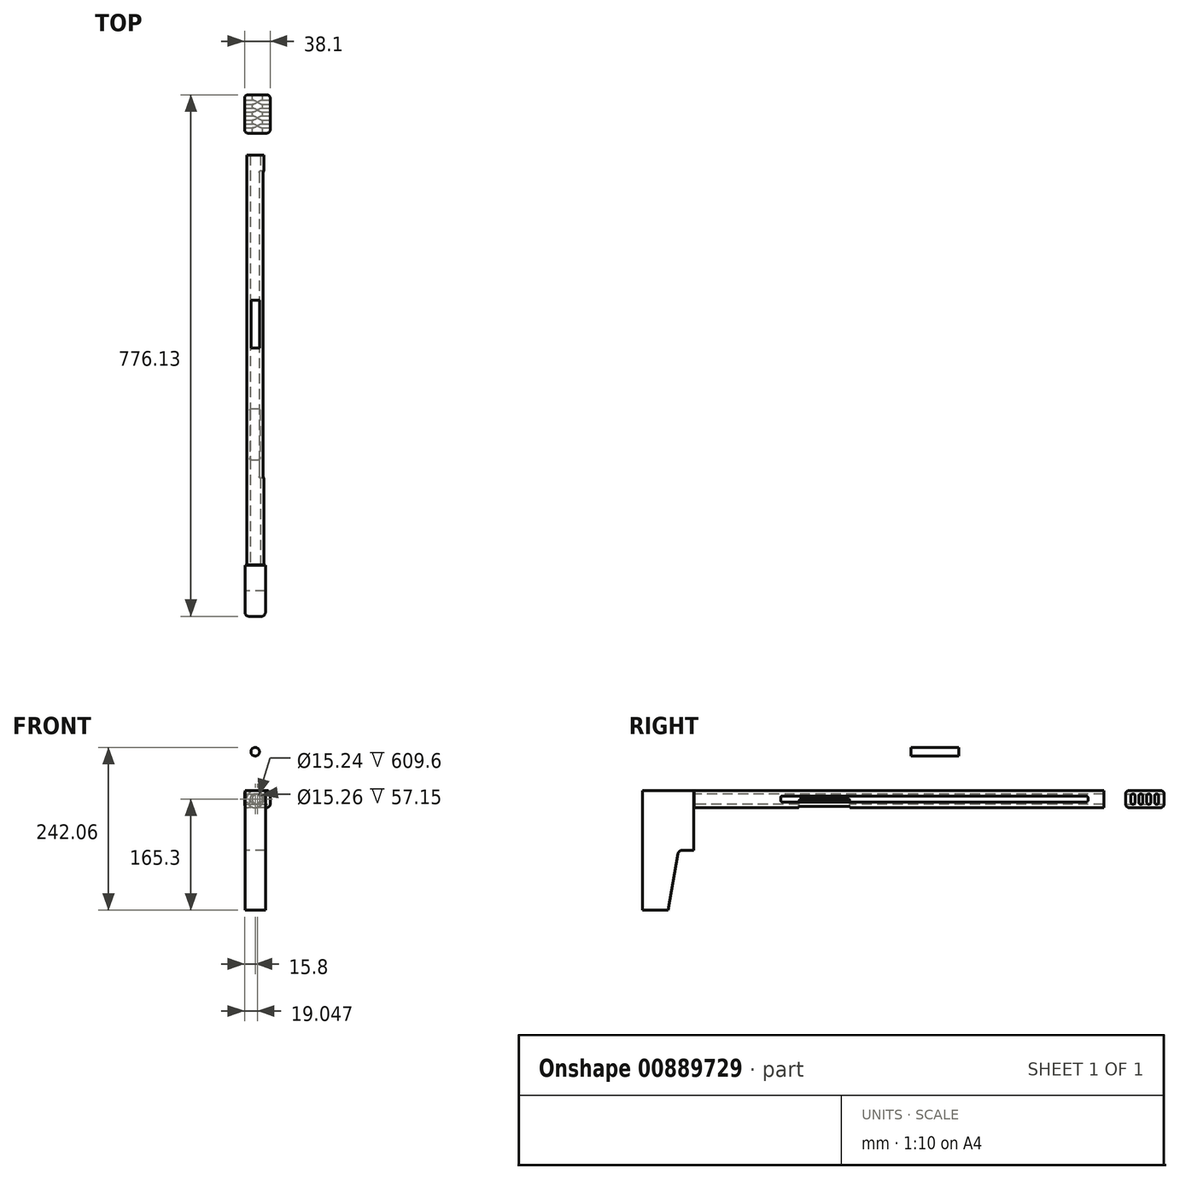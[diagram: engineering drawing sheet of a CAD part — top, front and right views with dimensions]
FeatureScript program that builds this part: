
annotation { "Feature Type Name" : "Feature", "Feature Type Description" : "" }
export const myFeature = defineFeature(function(context is Context, id is Id, definition is map)
    precondition{}
    {
        {
            var Q0;
            Q0=qCreatedBy(makeId("Right.planeOp"),FACE);
            var sketch = newSketch(context, id + "F0", { "sketchPlane" : qUnion([Q0])});
            skLineSegment(sketch, "E0.bottom", {"start": v(-36.5, 76.76) * mm, "end": v(34.62, 76.76) * mm});
            skLineSegment(sketch, "E0.top", {"start": v(-36.5, 64.06) * mm, "end": v(34.62, 64.06) * mm});
            skLineSegment(sketch, "E0.left", {"start": v(-36.5, 76.76) * mm, "end": v(-36.5, 64.06) * mm});
            skLineSegment(sketch, "E0.right", {"start": v(34.62, 76.76) * mm, "end": v(34.62, 64.06) * mm});
            skPoint(sketch, "E1", {"position": v(-36.5, 70.41) * mm});
            skPoint(sketch, "E2", {"position": v(34.62, 70.41) * mm});
            skLineSegment(sketch, "E3", {"start": v(-36.5, 70.41) * mm, "end": v(34.62, 70.41) * mm});
            skSolve(sketch);
        }
        {
            var Q0;
            Q0=qCreatedBy(makeId("Right.planeOp"),FACE);
            var sketch = newSketch(context, id + "F1", { "sketchPlane" : qUnion([Q0])});
            skLineSegment(sketch, "E4.bottom", {"start": v(-359.12, 12.55) * mm, "end": v(250.48, 12.55) * mm});
            skLineSegment(sketch, "E4.top", {"start": v(-359.12, -12.85) * mm, "end": v(250.48, -12.85) * mm});
            skLineSegment(sketch, "E4.left", {"start": v(-359.12, 12.55) * mm, "end": v(-359.12, -12.85) * mm});
            skLineSegment(sketch, "E4.right", {"start": v(250.48, 12.55) * mm, "end": v(250.48, -12.85) * mm});
            skPoint(sketch, "E5", {"position": v(-359.12, -0.15) * mm});
            skPoint(sketch, "E6", {"position": v(250.48, -0.15) * mm});
            skLineSegment(sketch, "E7", {"start": v(-359.12, -0.15) * mm, "end": v(250.48, -0.15) * mm});
            skSolve(sketch);
        }
        {
            var Q0;
            {var subQ0=sQuery(id+"F0.wireOp",EDGE,"E0.bottom");Q0=makeQuery(id+"F0.imprint","IMPRINT",FACE,{"disambiguationData":[TD([[makeQuery(id+"F0.imprint","IMPRINT",EDGE,{"derivedFrom":subQ0}),-1.0]])]});}
            var Q1;
            Q1=sQuery(id+"F0.wireOp",EDGE,"E3");
            revolve(context, id + "F2", {"surfaceOperationType" : NewSurfaceOperationType.NEW, "entities" : qUnion([Q0]), "axis" : qUnion([Q1]), "revolveType" : RevolveType.FULL});
        }
        {
            var Q0;
            {var subQ0=sQuery(id+"F1.wireOp",EDGE,"E4.bottom");Q0=makeQuery(id+"F1.imprint","IMPRINT",FACE,{"disambiguationData":[TD([[makeQuery(id+"F1.imprint","IMPRINT",EDGE,{"derivedFrom":subQ0}),-1.0]])]});}
            var Q1;
            Q1=sQuery(id+"F1.wireOp",EDGE,"E7");
            revolve(context, id + "F3", {"operationType" : NewBodyOperationType.ADD, "surfaceOperationType" : NewSurfaceOperationType.NEW, "entities" : qUnion([Q0]), "axis" : qUnion([Q1]), "revolveType" : RevolveType.FULL});
        }
        {
            var Q0;
            Q0=makeQuery(id+"F3.opRevolve","SWEPT_FACE",FACE,{"disambiguationData":[OSD([sQuery(id+"F1.wireOp",EDGE,"E4.left")])]});
            var sketch = newSketch(context, id + "F4", { "sketchPlane" : qUnion([Q0])});
            skPoint(sketch, "E8", {"position": v(0, 0) * mm});
            skCircle(sketch, "E9", {"center": v(0, 0) * mm, "radius": 7.62 * mm});
            skSolve(sketch);
        }
        {
            var Q0;
            Q0=makeQuery(id+"F4.imprint","IMPRINT",FACE,{"disambiguationData":[TD([[makeQuery(id+"F4.imprint","IMPRINT",EDGE,{"derivedFrom":sQuery(id+"F4.wireOp",EDGE,"E9")}),1.0]])]});
            extrude(context, id + "F5", {"entities" : qUnion([Q0]), "operationType" : NewBodyOperationType.REMOVE, "oppositeDirection" : true, "depth" : 649.48 * mm, "offsetDistance" : 25.4 * mm});
        }
        {
            var Q0;
            Q0=qCreatedBy(makeId("Right.planeOp"),FACE);
            var sketch = newSketch(context, id + "F6", { "sketchPlane" : qUnion([Q0])});
            skLineSegment(sketch, "E10.bottom", {"start": v(-359.7, 12.5) * mm, "end": v(-435.9, 12.5) * mm});
            skLineSegment(sketch, "E10.top", {"start": v(-359.7, -165.3) * mm, "end": v(-435.9, -165.3) * mm});
            skLineSegment(sketch, "E10.left", {"start": v(-359.7, 12.5) * mm, "end": v(-359.7, -165.3) * mm});
            skLineSegment(sketch, "E10.right", {"start": v(-435.9, 12.5) * mm, "end": v(-435.9, -165.3) * mm});
            skPoint(sketch, "E11", {"position": v(-397.8, -165.3) * mm});
            skPoint(sketch, "E12", {"position": v(-359.7, -76.4) * mm});
            skLineSegment(sketch, "E13", {"start": v(-359.7, -76.4) * mm, "end": v(-376.92, -76.4) * mm});
            skLineSegment(sketch, "E14", {"start": v(-383.18, -81.65) * mm, "end": v(-397.8, -165.3) * mm});
            skPoint(sketch, "E15.visualSharp", {"position": v(-382.26, -76.4) * mm});
            skArc(sketch, "E15.filletArc", {"start": v(-376.92, -76.4) * mm, "mid": v(-381, -77.89) * mm, "end": v(-383.18, -81.65) * mm});
            skSolve(sketch);
        }
        {
            var Q0;
            {var subQ1=sQuery(id+"F6.wireOp",EDGE,"E10.bottom");Q0=makeQuery(id+"F6.imprint","IMPRINT",FACE,{"disambiguationData":[TD([[makeQuery(id+"F6.imprint","IMPRINT",EDGE,{"derivedFrom":subQ1}),1.0]])]});}
            extrude(context, id + "F7", {"entities" : qUnion([Q0]), "depth" : 15.24 * mm, "offsetDistance" : 25.4 * mm, "hasSecondDirection" : true, "secondDirectionOppositeDirection" : true, "secondDirectionDepth" : 15.24 * mm});
        }
        {
            var Q0;
            Q0=makeQuery(id+"F7.opExtrude","SWEPT_FACE",FACE,{"disambiguationData":[OSD([sQuery(id+"F6.wireOp",EDGE,"E10.bottom")])]});
            var sketch = newSketch(context, id + "F8", { "sketchPlane" : qUnion([Q0])});
            skLineSegment(sketch, "E16.bottom", {"start": v(-8.9, -435.9) * mm, "end": v(8.89, -435.9) * mm});
            skArc(sketch, "E17.filletArc", {"start": v(-15.24, -429.54) * mm, "mid": v(-13.38, -434.03) * mm, "end": v(-8.9, -435.9) * mm});
            skArc(sketch, "E18.filletArc", {"start": v(8.89, -435.9) * mm, "mid": v(13.38, -434.03) * mm, "end": v(15.24, -429.54) * mm});
            skLineSegment(sketch, "E19", {"start": v(-15.24, -429.54) * mm, "end": v(-26.43, -429.54) * mm});
            skLineSegment(sketch, "E20", {"start": v(-26.43, -429.54) * mm, "end": v(-26.43, -444.21) * mm});
            skLineSegment(sketch, "E21", {"start": v(-26.43, -444.21) * mm, "end": v(23.72, -444.21) * mm});
            skLineSegment(sketch, "E22", {"start": v(23.72, -444.21) * mm, "end": v(23.72, -428.85) * mm});
            skLineSegment(sketch, "E23", {"start": v(23.72, -428.85) * mm, "end": v(15.24, -429.54) * mm});
            skLineSegment(sketch, "E24", {"start": v(-8.89, -435.9) * mm, "end": v(8.89, -435.9) * mm});
            skSolve(sketch);
        }
        {
            var Q0;
            Q0 = qSketchRegion(id + "F8", true);
            extrude(context, id + "F9", {"entities" : qUnion([Q0]), "operationType" : NewBodyOperationType.REMOVE, "oppositeDirection" : true, "depth" : 190 * mm, "offsetDistance" : 25.4 * mm});
        }
        {
            var Q0;
            Q0=qCreatedBy(makeId("Right.planeOp"),FACE);
            var sketch = newSketch(context, id + "F10", { "sketchPlane" : qUnion([Q0])});
            skLineSegment(sketch, "E25.bottom", {"start": v(-227.64, 4.57) * mm, "end": v(224.48, 4.57) * mm});
            skLineSegment(sketch, "E25.top", {"start": v(-227.64, -4.32) * mm, "end": v(224.48, -4.32) * mm});
            skLineSegment(sketch, "E25.left", {"start": v(-230.18, 2.03) * mm, "end": v(-230.18, -1.78) * mm});
            skLineSegment(sketch, "E25.right", {"start": v(227.02, 2.03) * mm, "end": v(227.02, -1.78) * mm});
            skPoint(sketch, "E26.visualSharp", {"position": v(-230.18, 4.57) * mm});
            skArc(sketch, "E26.filletArc", {"start": v(-227.64, 4.57) * mm, "mid": v(-229.44, 3.83) * mm, "end": v(-230.18, 2.03) * mm});
            skPoint(sketch, "E27.visualSharp", {"position": v(-230.18, -4.32) * mm});
            skArc(sketch, "E27.filletArc", {"start": v(-230.18, -1.78) * mm, "mid": v(-229.44, -3.57) * mm, "end": v(-227.64, -4.32) * mm});
            skPoint(sketch, "E28.visualSharp", {"position": v(227.02, -4.32) * mm});
            skArc(sketch, "E28.filletArc", {"start": v(224.48, -4.32) * mm, "mid": v(226.27, -3.57) * mm, "end": v(227.02, -1.78) * mm});
            skPoint(sketch, "E29.visualSharp", {"position": v(227.02, 4.57) * mm});
            skArc(sketch, "E29.filletArc", {"start": v(227.02, 2.03) * mm, "mid": v(226.27, 3.83) * mm, "end": v(224.48, 4.57) * mm});
            skSolve(sketch);
        }
        {
            var Q0;
            Q0 = qSketchRegion(id + "F10", true);
            extrude(context, id + "F11", {"entities" : qUnion([Q0]), "operationType" : NewBodyOperationType.REMOVE, "depth" : 25.4 * mm, "offsetDistance" : 25.4 * mm});
        }
        {
            var Q0;
            Q0=qCreatedBy(makeId("Top.planeOp"),FACE);
            var sketch = newSketch(context, id + "F12", { "sketchPlane" : qUnion([Q0])});
            skLineSegment(sketch, "E30.bottom", {"start": v(-8.08, -200.68) * mm, "end": v(-8.08, -129.56) * mm});
            skLineSegment(sketch, "E30.top", {"start": v(7.16, -200.68) * mm, "end": v(7.16, -129.56) * mm});
            skLineSegment(sketch, "E30.left", {"start": v(-5.54, -203.22) * mm, "end": v(4.62, -203.22) * mm});
            skLineSegment(sketch, "E30.right", {"start": v(-5.54, -127.02) * mm, "end": v(4.62, -127.02) * mm});
            skPoint(sketch, "E31.visualSharp", {"position": v(-8.08, -203.22) * mm});
            skArc(sketch, "E31.filletArc", {"start": v(-8.08, -200.68) * mm, "mid": v(-7.34, -202.47) * mm, "end": v(-5.54, -203.22) * mm});
            skPoint(sketch, "E32.visualSharp", {"position": v(7.16, -203.22) * mm});
            skArc(sketch, "E32.filletArc", {"start": v(4.62, -203.22) * mm, "mid": v(6.41, -202.47) * mm, "end": v(7.16, -200.68) * mm});
            skPoint(sketch, "E33.visualSharp", {"position": v(7.16, -127.02) * mm});
            skArc(sketch, "E33.filletArc", {"start": v(7.16, -129.56) * mm, "mid": v(6.41, -127.76) * mm, "end": v(4.62, -127.02) * mm});
            skPoint(sketch, "E34.visualSharp", {"position": v(-8.08, -127.02) * mm});
            skArc(sketch, "E34.filletArc", {"start": v(-5.54, -127.02) * mm, "mid": v(-7.34, -127.76) * mm, "end": v(-8.08, -129.56) * mm});
            skSolve(sketch);
        }
        {
            var Q0;
            Q0=makeQuery(id+"F12.imprint","IMPRINT",FACE,{"disambiguationData":[TD([[makeQuery(id+"F12.imprint","IMPRINT",EDGE,{"derivedFrom":sQuery(id+"F12.wireOp",EDGE,"E30.bottom")}),-1.0]])]});
            extrude(context, id + "F13", {"entities" : qUnion([Q0]), "operationType" : NewBodyOperationType.REMOVE, "oppositeDirection" : true, "depth" : 25.4 * mm, "offsetDistance" : 25.4 * mm});
        }
        {
            var Q0;
            Q0=qCreatedBy(makeId("Top.planeOp"),FACE);
            var sketch = newSketch(context, id + "F14", { "sketchPlane" : qUnion([Q0])});
            skLineSegment(sketch, "E35.bottom", {"start": v(22.3, 283.1) * mm, "end": v(-15.8, 283.1) * mm});
            skLineSegment(sketch, "E35.top", {"start": v(22.3, 340.24) * mm, "end": v(-15.8, 340.24) * mm});
            skLineSegment(sketch, "E35.left", {"start": v(22.3, 283.1) * mm, "end": v(22.3, 340.24) * mm});
            skLineSegment(sketch, "E35.right", {"start": v(-15.8, 283.1) * mm, "end": v(-15.8, 340.24) * mm});
            skSolve(sketch);
        }
        {
            var Q0;
            Q0 = qSketchRegion(id + "F14", true);
            extrude(context, id + "F15", {"entities" : qUnion([Q0]), "depth" : 12.7 * mm, "offsetDistance" : 25.4 * mm, "hasSecondDirection" : true, "secondDirectionOppositeDirection" : true, "secondDirectionDepth" : 12.7 * mm});
        }
        {
            var Q0;
            Q0=makeQuery(id+"F15.opExtrude","CAP_EDGE",EDGE,{"disambiguationData":[OSD([sQuery(id+"F14.wireOp",EDGE,"E35.right")])],"isStart":false});
            var Q1;
            Q1=makeQuery(id+"F15.opExtrude","CAP_EDGE",EDGE,{"disambiguationData":[OSD([sQuery(id+"F14.wireOp",EDGE,"E35.right")])],"isStart":true});
            var Q2;
            Q2=makeQuery(id+"F15.opExtrude","CAP_EDGE",EDGE,{"disambiguationData":[OSD([sQuery(id+"F14.wireOp",EDGE,"E35.left")])],"isStart":true});
            var Q3;
            Q3=makeQuery(id+"F15.opExtrude","CAP_EDGE",EDGE,{"disambiguationData":[OSD([sQuery(id+"F14.wireOp",EDGE,"E35.left")])],"isStart":false});
            var Q4;
            Q4=makeQuery(id+"F15.opExtrude","CAP_EDGE",EDGE,{"disambiguationData":[OSD([sQuery(id+"F14.wireOp",EDGE,"E35.top")])],"isStart":false});
            var Q5;
            Q5=makeQuery(id+"F15.opExtrude","CAP_EDGE",EDGE,{"disambiguationData":[OSD([sQuery(id+"F14.wireOp",EDGE,"E35.top")])],"isStart":true});
            var Q6;
            Q6=makeQuery(id+"F15.opExtrude","SWEPT_EDGE",EDGE,{"disambiguationData":[OSD([sQuery(id+"F14.wireOp",EDGE,"E35.top"),sQuery(id+"F14.wireOp",EDGE,"E35.left")])]});
            var Q7;
            Q7=makeQuery(id+"F15.opExtrude","SWEPT_EDGE",EDGE,{"disambiguationData":[OSD([sQuery(id+"F14.wireOp",EDGE,"E35.top"),sQuery(id+"F14.wireOp",EDGE,"E35.right")])]});
            var Q8;
            Q8=makeQuery(id+"F15.opExtrude","SWEPT_FACE",FACE,{"disambiguationData":[OSD([sQuery(id+"F14.wireOp",EDGE,"E35.right")])]});
            var Q9;
            Q9=makeQuery(id+"F15.opExtrude","SWEPT_EDGE",EDGE,{"disambiguationData":[OSD([sQuery(id+"F14.wireOp",EDGE,"E35.bottom"),sQuery(id+"F14.wireOp",EDGE,"E35.left")])]});
            var Q10;
            Q10=makeQuery(id+"F15.opExtrude","CAP_EDGE",EDGE,{"disambiguationData":[OSD([sQuery(id+"F14.wireOp",EDGE,"E35.bottom")])],"isStart":false});
            var Q11;
            Q11=makeQuery(id+"F15.opExtrude","CAP_EDGE",EDGE,{"disambiguationData":[OSD([sQuery(id+"F14.wireOp",EDGE,"E35.bottom")])],"isStart":true});
            fillet(context, id + "F16", {"entities" : qUnion([Q0, Q1, Q2, Q3, Q4, Q5, Q6, Q7, Q8, Q9, Q10, Q11]), "radius" : 5.08 * mm, "tangentPropagation" : true, "allowEdgeOverflow" : false});
        }
        {
            var Q0;
            Q0=makeQuery(id+"F15.opExtrude","SWEPT_FACE",FACE,{"disambiguationData":[OSD([sQuery(id+"F14.wireOp",EDGE,"E35.left")])]});
            var sketch = newSketch(context, id + "F17", { "sketchPlane" : qUnion([Q0])});
            skPoint(sketch, "E36", {"position": v(314.51, 7.62) * mm});
            skPoint(sketch, "E37", {"position": v(302.77, 7.62) * mm});
            skPoint(sketch, "E38", {"position": v(326.26, 7.62) * mm});
            skPoint(sketch, "E39", {"position": v(308.64, 7.62) * mm});
            skPoint(sketch, "E40", {"position": v(320.39, 7.62) * mm});
            skPoint(sketch, "E41", {"position": v(332.14, 7.62) * mm});
            skLineSegment(sketch, "E42", {"start": v(302.77, 5.08) * mm, "end": v(302.77, -5.08) * mm});
            skLineSegment(sketch, "E43", {"start": v(308.64, 5.08) * mm, "end": v(308.64, -5.08) * mm});
            skLineSegment(sketch, "E44", {"start": v(314.51, 5.08) * mm, "end": v(314.51, -5.08) * mm});
            skLineSegment(sketch, "E45", {"start": v(320.39, 5.08) * mm, "end": v(320.39, -5.08) * mm});
            skLineSegment(sketch, "E46", {"start": v(326.26, 5.08) * mm, "end": v(326.26, -5.08) * mm});
            skLineSegment(sketch, "E47", {"start": v(332.14, 5.08) * mm, "end": v(332.14, -5.08) * mm});
            skLineSegment(sketch, "E48", {"start": v(305.3, 7.62) * mm, "end": v(306.1, 7.62) * mm});
            skLineSegment(sketch, "E49", {"start": v(306.1, -7.62) * mm, "end": v(305.3, -7.62) * mm});
            skLineSegment(sketch, "E50", {"start": v(317.05, -7.62) * mm, "end": v(317.85, -7.62) * mm});
            skLineSegment(sketch, "E51", {"start": v(317.85, 7.62) * mm, "end": v(317.05, 7.62) * mm});
            skLineSegment(sketch, "E52", {"start": v(328.8, 7.62) * mm, "end": v(329.6, 7.62) * mm});
            skLineSegment(sketch, "E53", {"start": v(329.6, -7.62) * mm, "end": v(328.8, -7.62) * mm});
            skArc(sketch, "E54.filletArc", {"start": v(308.64, 5.08) * mm, "mid": v(307.9, 6.88) * mm, "end": v(306.1, 7.62) * mm});
            skArc(sketch, "E55.filletArc", {"start": v(305.3, 7.62) * mm, "mid": v(303.51, 6.88) * mm, "end": v(302.77, 5.08) * mm});
            skArc(sketch, "E56.filletArc", {"start": v(317.05, 7.62) * mm, "mid": v(315.26, 6.88) * mm, "end": v(314.51, 5.08) * mm});
            skArc(sketch, "E57.filletArc", {"start": v(320.39, 5.08) * mm, "mid": v(319.64, 6.88) * mm, "end": v(317.85, 7.62) * mm});
            skArc(sketch, "E58.filletArc", {"start": v(328.8, 7.62) * mm, "mid": v(327, 6.88) * mm, "end": v(326.26, 5.08) * mm});
            skArc(sketch, "E59.filletArc", {"start": v(332.14, 5.08) * mm, "mid": v(331.4, 6.88) * mm, "end": v(329.6, 7.62) * mm});
            skPoint(sketch, "E60.visualSharp", {"position": v(332.14, -7.62) * mm});
            skArc(sketch, "E60.filletArc", {"start": v(329.6, -7.62) * mm, "mid": v(331.4, -6.88) * mm, "end": v(332.14, -5.08) * mm});
            skPoint(sketch, "E61.visualSharp", {"position": v(326.26, -7.62) * mm});
            skArc(sketch, "E61.filletArc", {"start": v(326.26, -5.08) * mm, "mid": v(327, -6.88) * mm, "end": v(328.8, -7.62) * mm});
            skPoint(sketch, "E62.visualSharp", {"position": v(320.39, -7.62) * mm});
            skArc(sketch, "E62.filletArc", {"start": v(317.85, -7.62) * mm, "mid": v(319.64, -6.88) * mm, "end": v(320.39, -5.08) * mm});
            skPoint(sketch, "E63.visualSharp", {"position": v(314.51, -7.62) * mm});
            skArc(sketch, "E63.filletArc", {"start": v(314.51, -5.08) * mm, "mid": v(315.26, -6.88) * mm, "end": v(317.05, -7.62) * mm});
            skPoint(sketch, "E64.visualSharp", {"position": v(308.64, -7.62) * mm});
            skArc(sketch, "E64.filletArc", {"start": v(306.1, -7.62) * mm, "mid": v(307.9, -6.88) * mm, "end": v(308.64, -5.08) * mm});
            skPoint(sketch, "E65.visualSharp", {"position": v(302.77, -7.62) * mm});
            skArc(sketch, "E65.filletArc", {"start": v(302.77, -5.08) * mm, "mid": v(303.51, -6.88) * mm, "end": v(305.3, -7.62) * mm});
            skPoint(sketch, "E66", {"position": v(296.9, 7.62) * mm});
            skPoint(sketch, "E67", {"position": v(291.02, 7.62) * mm});
            skLineSegment(sketch, "E68", {"start": v(296.9, 5.08) * mm, "end": v(296.9, -5.08) * mm});
            skLineSegment(sketch, "E69", {"start": v(294.35, -7.62) * mm, "end": v(293.56, -7.62) * mm});
            skLineSegment(sketch, "E70", {"start": v(291.02, -5.08) * mm, "end": v(291.02, 5.08) * mm});
            skLineSegment(sketch, "E71", {"start": v(294.35, 7.62) * mm, "end": v(293.56, 7.62) * mm});
            skArc(sketch, "E72.filletArc", {"start": v(293.56, 7.62) * mm, "mid": v(291.76, 6.88) * mm, "end": v(291.02, 5.08) * mm});
            skArc(sketch, "E73.filletArc", {"start": v(296.9, 5.08) * mm, "mid": v(296.15, 6.88) * mm, "end": v(294.35, 7.62) * mm});
            skPoint(sketch, "E74.visualSharp", {"position": v(296.9, -7.62) * mm});
            skArc(sketch, "E74.filletArc", {"start": v(294.35, -7.62) * mm, "mid": v(296.15, -6.88) * mm, "end": v(296.9, -5.08) * mm});
            skPoint(sketch, "E75.visualSharp", {"position": v(291.02, -7.62) * mm});
            skArc(sketch, "E75.filletArc", {"start": v(291.02, -5.08) * mm, "mid": v(291.76, -6.88) * mm, "end": v(293.56, -7.62) * mm});
            skSolve(sketch);
        }
        {
            var Q0;
            Q0 = qSketchRegion(id + "F17", true);
            extrude(context, id + "F18", {"entities" : qUnion([Q0]), "operationType" : NewBodyOperationType.REMOVE, "oppositeDirection" : true, "depth" : 52.78 * mm, "offsetDistance" : 25.4 * mm});
        }
        {
            var Q0;
            Q0=makeQuery(id+"F15.opExtrude","SWEPT_FACE",FACE,{"disambiguationData":[OSD([sQuery(id+"F14.wireOp",EDGE,"E35.top")])]});
            var sketch = newSketch(context, id + "F19", { "sketchPlane" : qUnion([Q0])});
            skCircle(sketch, "E76", {"center": v(-3.25, 0) * mm, "radius": 7.63 * mm});
            skSolve(sketch);
        }
        {
            var Q0;
            Q0 = qSketchRegion(id + "F19", true);
            extrude(context, id + "F20", {"entities" : qUnion([Q0]), "operationType" : NewBodyOperationType.REMOVE, "oppositeDirection" : true, "depth" : 70.1 * mm, "offsetDistance" : 25.4 * mm});
        }
    });
